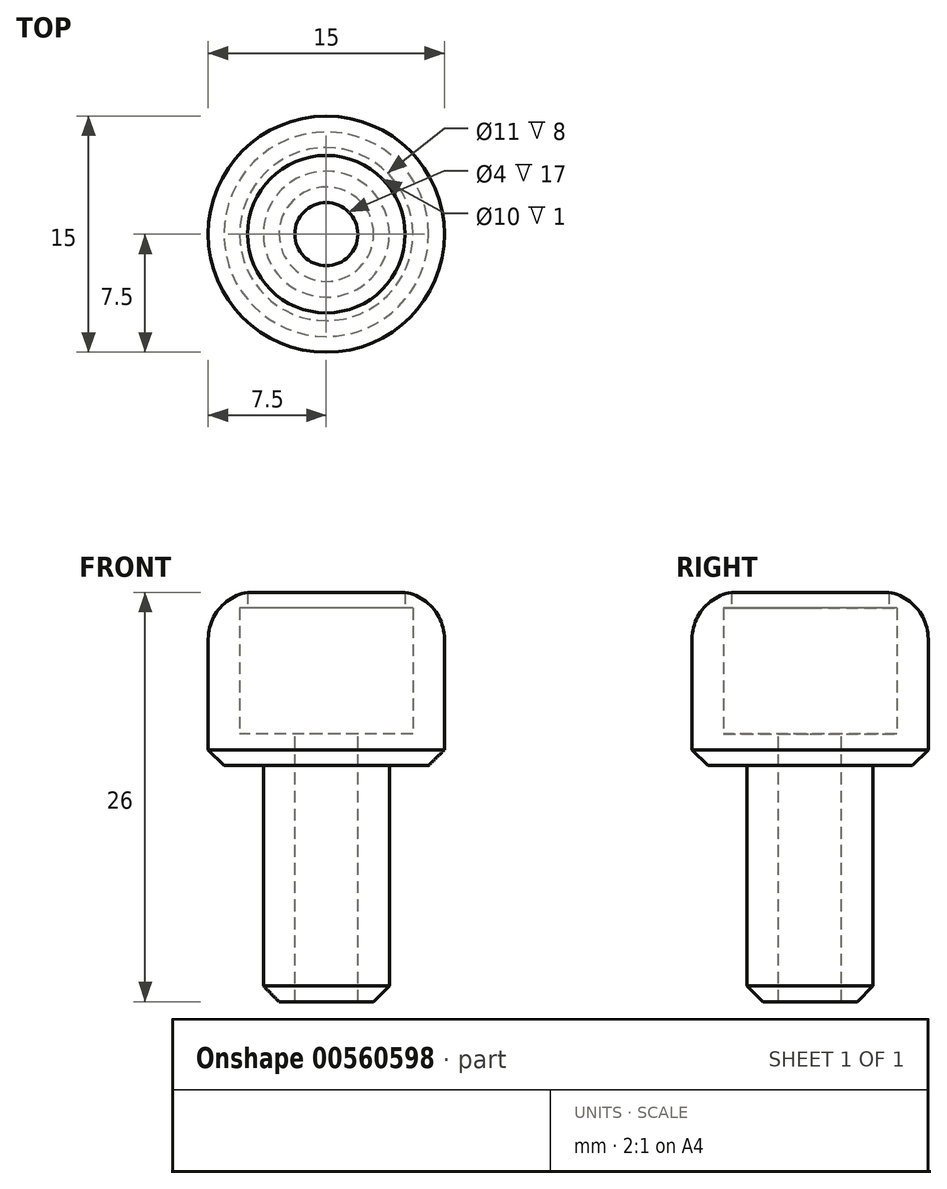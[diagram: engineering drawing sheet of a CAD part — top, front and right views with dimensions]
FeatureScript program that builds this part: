
annotation { "Feature Type Name" : "Feature", "Feature Type Description" : "" }
export const myFeature = defineFeature(function(context is Context, id is Id, definition is map)
    precondition{}
    {
        {
            var Q0;
            Q0=qCreatedBy(makeId("Top.planeOp"),FACE);
            var sketch = newSketch(context, id + "F0", { "sketchPlane" : qUnion([Q0])});
            skCircle(sketch, "E0", {"center": v(0, 0) * mm, "radius": 7.5 * mm});
            skSolve(sketch);
        }
        {
            var Q0;
            Q0=makeQuery(id+"F0.imprint","IMPRINT",FACE,{"disambiguationData":[TD([[makeQuery(id+"F0.imprint","IMPRINT",EDGE,{"derivedFrom":sQuery(id+"F0.wireOp",EDGE,"E0")}),1.0]])]});
            extrude(context, id + "F1", {"entities" : qUnion([Q0]), "depth" : 10 * mm, "offsetDistance" : 25 * mm});
        }
        {
            var Q0;
            Q0=makeQuery(id+"F1.opExtrude","CAP_FACE",FACE,{"disambiguationData":[OSD([sQuery(id+"F0.wireOp",EDGE,"E0")])],"isStart":true});
            var sketch = newSketch(context, id + "F2", { "sketchPlane" : qUnion([Q0])});
            skCircle(sketch, "E1", {"center": v(0, 0) * mm, "radius": 4 * mm});
            skSolve(sketch);
        }
        {
            var Q0;
            Q0=makeQuery(id+"F2.imprint","IMPRINT",FACE,{"disambiguationData":[TD([[makeQuery(id+"F2.imprint","IMPRINT",EDGE,{"derivedFrom":sQuery(id+"F2.wireOp",EDGE,"E1")}),1.0]])]});
            extrude(context, id + "F3", {"entities" : qUnion([Q0]), "operationType" : NewBodyOperationType.ADD, "depth" : 15 * mm, "offsetDistance" : 25 * mm});
        }
        {
            var Q0;
            Q0=makeQuery(id+"F1.opExtrude","CAP_FACE",FACE,{"disambiguationData":[OSD([sQuery(id+"F0.wireOp",EDGE,"E0")])],"isStart":false});
            var Q1;
            Q1=makeQuery(id+"F3.opExtrude","CAP_FACE",FACE,{"disambiguationData":[OSD([sQuery(id+"F2.wireOp",EDGE,"E1")])],"isStart":false});
            shell(context, id + "F4", {"entities" : qUnion([Q0, Q1]), "thickness" : 2 * mm});
        }
        {
            var Q0;
            Q0=makeQuery(id+"F1.opExtrude","CAP_FACE",FACE,{"disambiguationData":[OSD([sQuery(id+"F0.wireOp",EDGE,"E0")])],"isStart":false});
            var sketch = newSketch(context, id + "F5", { "sketchPlane" : qUnion([Q0])});
            skCircle(sketch, "E2", {"center": v(0, 0) * mm, "radius": 7.5 * mm});
            skCircle(sketch, "E3", {"center": v(0, 0) * mm, "radius": 5 * mm});
            skSolve(sketch);
        }
        {
            var Q0;
            Q0 = qSketchRegion(id + "F5", true);
            extrude(context, id + "F6", {"entities" : qUnion([Q0]), "operationType" : NewBodyOperationType.ADD, "depth" : 1 * mm, "offsetDistance" : 25 * mm});
        }
        {
            var Q0;
            Q0=makeQuery(id+"F6.opExtrude","CAP_EDGE",EDGE,{"disambiguationData":[OSD([sQuery(id+"F5.wireOp",EDGE,"E2")])],"isStart":false});
            fillet(context, id + "F7", {"entities" : qUnion([Q0]), "radius" : 3 * mm, "tangentPropagation" : true, "allowEdgeOverflow" : false});
        }
        {
            var Q0;
            Q0=makeQuery(id+"F1.opExtrude","CAP_EDGE",EDGE,{"disambiguationData":[OSD([sQuery(id+"F0.wireOp",EDGE,"E0")])],"isStart":true});
            chamfer(context, id + "F8", {"entities" : qUnion([Q0]), "width" : 1 * mm, "tangentPropagation" : true});
        }
        {
            var Q0;
            Q0=makeQuery(id+"F3.opExtrude","CAP_EDGE",EDGE,{"disambiguationData":[OSD([sQuery(id+"F2.wireOp",EDGE,"E1")])],"isStart":false});
            chamfer(context, id + "F9", {"entities" : qUnion([Q0]), "width" : 1 * mm, "tangentPropagation" : true});
        }
    });
